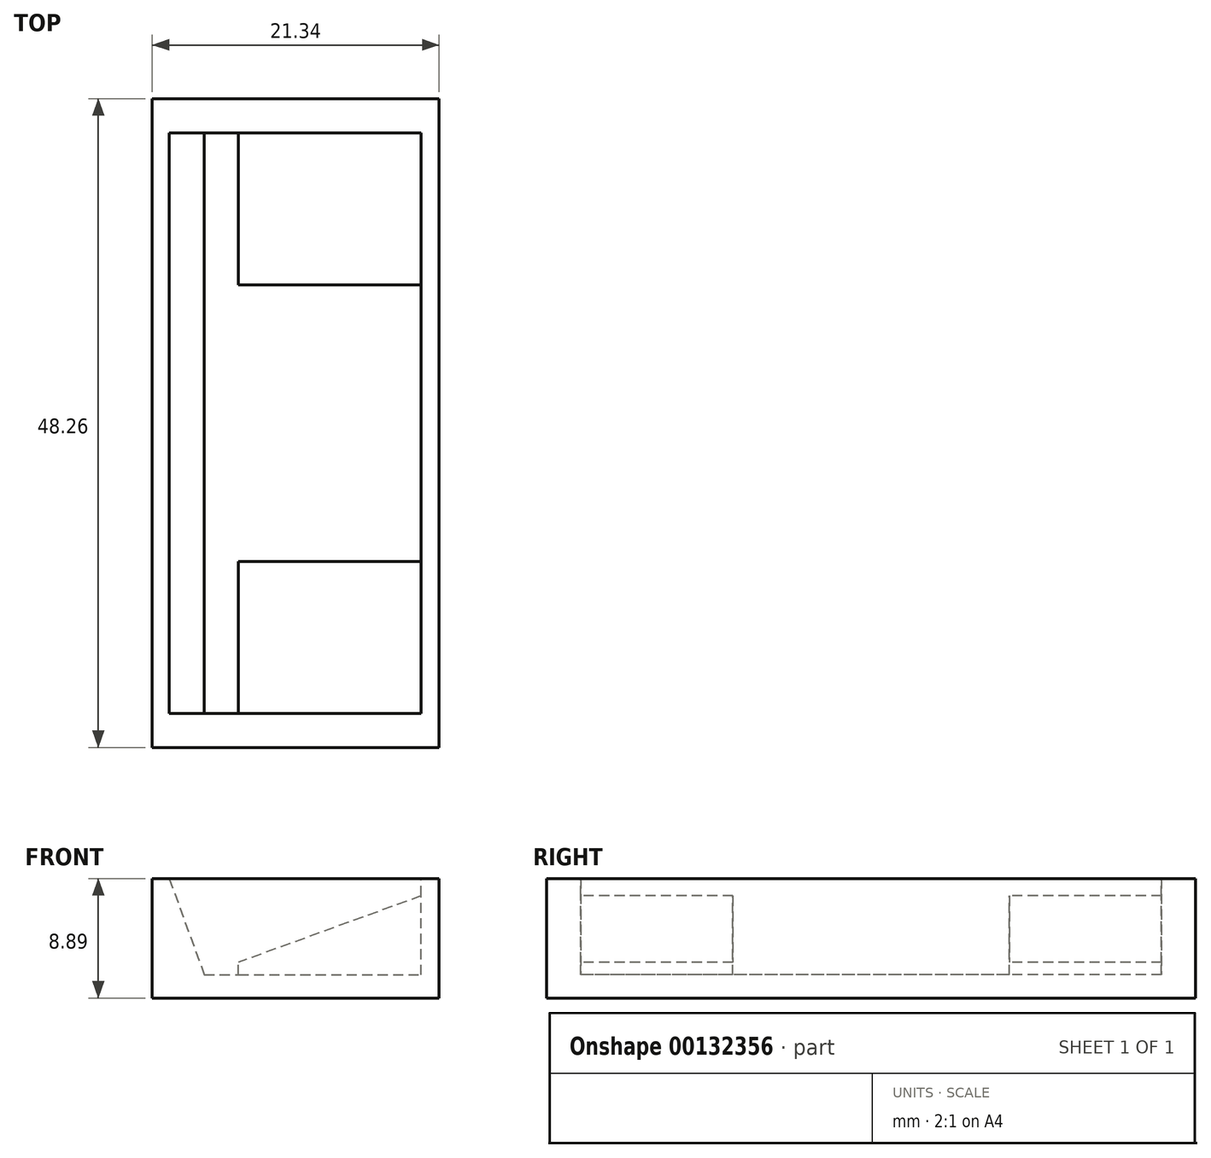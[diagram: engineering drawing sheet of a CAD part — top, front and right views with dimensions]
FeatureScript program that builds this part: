
annotation { "Feature Type Name" : "Feature", "Feature Type Description" : "" }
export const myFeature = defineFeature(function(context is Context, id is Id, definition is map)
    precondition{}
    {
        {
            var Q0;
            Q0=qCreatedBy(makeId("Front.planeOp"),FACE);
            var sketch = newSketch(context, id + "F0", { "sketchPlane" : qUnion([Q0])});
            skLineSegment(sketch, "E0.bottom", {"start": v(0, 0) * mm, "end": v(21.34, 0) * mm});
            skLineSegment(sketch, "E0.top", {"start": v(0, 8.89) * mm, "end": v(21.34, 8.89) * mm});
            skLineSegment(sketch, "E0.left", {"start": v(0, 0) * mm, "end": v(0, 8.89) * mm});
            skLineSegment(sketch, "E0.right", {"start": v(21.34, 0) * mm, "end": v(21.34, 8.89) * mm});
            skSolve(sketch);
        }
        {
            var Q0;
            Q0=makeQuery(id+"F0.imprint","IMPRINT",FACE,{"disambiguationData":[TD([[makeQuery(id+"F0.imprint","IMPRINT",EDGE,{"derivedFrom":sQuery(id+"F0.wireOp",EDGE,"E0.bottom")}),1.0]])]});
            extrude(context, id + "F1", {"entities" : qUnion([Q0]), "endBound" : BoundingType.SYMMETRIC, "depth" : 48.26 * mm});
        }
        {
            var Q0;
            Q0=qCreatedBy(makeId("Front.planeOp"),FACE);
            var sketch = newSketch(context, id + "F2", { "sketchPlane" : qUnion([Q0])});
            skLineSegment(sketch, "E1", {"start": v(1.27, 8.89) * mm, "end": v(3.88, 1.73) * mm});
            skLineSegment(sketch, "E2", {"start": v(3.88, 1.73) * mm, "end": v(6.42, 1.73) * mm});
            skLineSegment(sketch, "E3", {"start": v(3.88, 1.73) * mm, "end": v(19.99, 7.6) * mm, "construction": true});
            skLineSegment(sketch, "E4", {"start": v(6.42, 1.73) * mm, "end": v(6.42, 2.65) * mm});
            skLineSegment(sketch, "E5", {"start": v(6.42, 2.65) * mm, "end": v(19.99, 7.6) * mm});
            skLineSegment(sketch, "E6", {"start": v(19.99, 7.6) * mm, "end": v(19.99, 8.89) * mm});
            skLineSegment(sketch, "E7", {"start": v(19.99, 8.89) * mm, "end": v(1.27, 8.89) * mm});
            skSolve(sketch);
        }
        {
            var Q0;
            Q0 = qSketchRegion(id + "F2", true);
            extrude(context, id + "F3", {"entities" : qUnion([Q0]), "operationType" : NewBodyOperationType.REMOVE, "endBound" : BoundingType.SYMMETRIC, "oppositeDirection" : true, "depth" : 43.18 * mm});
        }
        {
            var Q0;
            Q0=qCreatedBy(makeId("Front.planeOp"),FACE);
            var sketch = newSketch(context, id + "F4", { "sketchPlane" : qUnion([Q0])});
            skLineSegment(sketch, "E8.bottom", {"start": v(6.42, 1.73) * mm, "end": v(19.99, 1.73) * mm});
            skLineSegment(sketch, "E8.top", {"start": v(6.42, 10.66) * mm, "end": v(19.99, 10.66) * mm});
            skLineSegment(sketch, "E8.left", {"start": v(6.42, 1.73) * mm, "end": v(6.42, 10.66) * mm});
            skLineSegment(sketch, "E8.right", {"start": v(19.99, 1.73) * mm, "end": v(19.99, 10.66) * mm});
            skSolve(sketch);
        }
        {
            var Q0;
            Q0 = qSketchRegion(id + "F4", true);
            extrude(context, id + "F5", {"entities" : qUnion([Q0]), "operationType" : NewBodyOperationType.REMOVE, "endBound" : BoundingType.SYMMETRIC, "oppositeDirection" : true, "depth" : 20.57 * mm});
        }
    });
